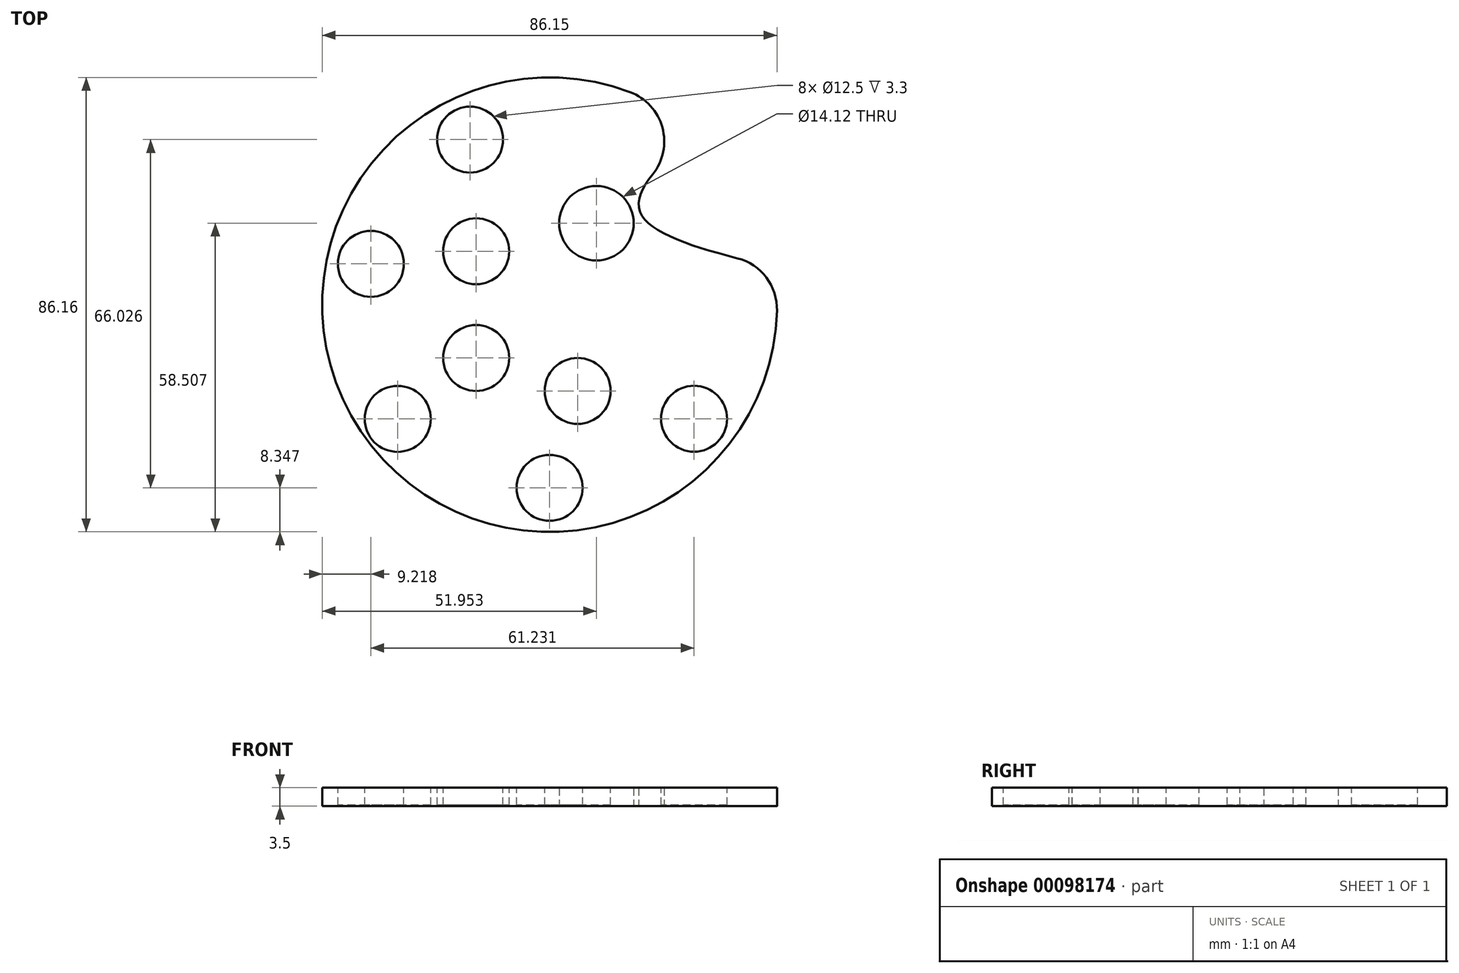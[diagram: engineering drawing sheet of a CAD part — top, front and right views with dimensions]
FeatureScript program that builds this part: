
annotation { "Feature Type Name" : "Feature", "Feature Type Description" : "" }
export const myFeature = defineFeature(function(context is Context, id is Id, definition is map)
    precondition{}
    {
        {
            var Q0;
            Q0=qCreatedBy(makeId("Top.planeOp"),FACE);
            var sketch = newSketch(context, id + "F0", { "sketchPlane" : qUnion([Q0])});
            skArc(sketch, "E0", {"start": v(27.73, 32.97) * mm, "mid": v(-37.42, -21.34) * mm, "end": v(42.5, 7.08) * mm});
            skFitSpline(sketch, "E1", {"points": [v(27.73, 32.97) * mm, v(17, 17.93) * mm, v(42.5, 7.08) * mm], "startDerivative": vector(-39.63, -36.53) * mm, "endDerivative": vector(65.58, -15.93) * mm});
            skSolve(sketch);
        }
        {
            var Q0;
            Q0 = qSketchRegion(id + "F0", true);
            extrude(context, id + "F1", {"entities" : qUnion([Q0]), "depth" : 3.5 * mm});
        }
        {
            var Q0;
            Q0=qCreatedBy(makeId("Top.planeOp"),FACE);
            var sketch = newSketch(context, id + "F2", { "sketchPlane" : qUnion([Q0])});
            skCircle(sketch, "E2", {"center": v(8.87, 15.43) * mm, "radius": 7.06 * mm});
            skSolve(sketch);
        }
        {
            var Q0;
            Q0=makeQuery(id+"F2.imprint","IMPRINT",FACE,{"disambiguationData":[TD([[makeQuery(id+"F2.imprint","IMPRINT",EDGE,{"derivedFrom":sQuery(id+"F2.wireOp",EDGE,"E2")}),1.0]])]});
            extrude(context, id + "F3", {"entities" : qUnion([Q0]), "operationType" : NewBodyOperationType.REMOVE, "depth" : 25 * mm});
        }
        {
            var Q0;
            Q0=makeQuery(id+"F1.opExtrude","CAP_FACE",FACE,{"disambiguationData":[OSD([sQuery(id+"F0.wireOp",EDGE,"E0"),sQuery(id+"F0.wireOp",EDGE,"E1")])],"isStart":false});
            var sketch = newSketch(context, id + "F4", { "sketchPlane" : qUnion([Q0])});
            skCircle(sketch, "E3.cCircle", {"center": v(0, 0) * mm, "radius": 31.3 * mm, "construction": true});
            skLineSegment(sketch, "E3.0", {"start": v(-15.07, 31.3) * mm, "end": v(15.07, 31.3) * mm, "construction": true});
            skLineSegment(sketch, "E3.1", {"start": v(15.07, 31.3) * mm, "end": v(33.86, 7.73) * mm, "construction": true});
            skLineSegment(sketch, "E3.2", {"start": v(33.86, 7.73) * mm, "end": v(27.16, -21.66) * mm, "construction": true});
            skLineSegment(sketch, "E3.3", {"start": v(27.16, -21.66) * mm, "end": v(0, -34.73) * mm, "construction": true});
            skLineSegment(sketch, "E3.4", {"start": v(0, -34.73) * mm, "end": v(-27.16, -21.66) * mm, "construction": true});
            skLineSegment(sketch, "E3.5", {"start": v(-27.16, -21.66) * mm, "end": v(-33.86, 7.73) * mm, "construction": true});
            skLineSegment(sketch, "E3.6", {"start": v(-33.86, 7.73) * mm, "end": v(-15.07, 31.3) * mm, "construction": true});
            skPoint(sketch, "E3.0.midPoint", {"position": v(0, 31.3) * mm});
            skCircle(sketch, "E4", {"center": v(-15.07, 31.3) * mm, "radius": 6.25 * mm});
            skCircle(sketch, "E5", {"center": v(-33.86, 7.73) * mm, "radius": 6.25 * mm});
            skCircle(sketch, "E6", {"center": v(-28.78, -21.66) * mm, "radius": 6.25 * mm});
            skCircle(sketch, "E7", {"center": v(0, -34.73) * mm, "radius": 6.25 * mm});
            skCircle(sketch, "E8", {"center": v(27.37, -21.63) * mm, "radius": 6.25 * mm});
            skSolve(sketch);
        }
        {
            var Q0;
            Q0 = qSketchRegion(id + "F4", true);
            extrude(context, id + "F5", {"entities" : qUnion([Q0]), "operationType" : NewBodyOperationType.REMOVE, "oppositeDirection" : true, "depth" : 3.3 * mm});
        }
        {
            var Q0;
            Q0=makeQuery(id+"F1.opExtrude","CAP_FACE",FACE,{"disambiguationData":[OSD([sQuery(id+"F0.wireOp",EDGE,"E0"),sQuery(id+"F0.wireOp",EDGE,"E1")])],"isStart":false});
            var sketch = newSketch(context, id + "F6", { "sketchPlane" : qUnion([Q0])});
            skCircle(sketch, "E9.cCircle", {"center": v(0, 0) * mm, "radius": 16.36 * mm, "construction": true});
            skLineSegment(sketch, "E9.0", {"start": v(-5.32, 16.36) * mm, "end": v(5.32, 16.36) * mm, "construction": true});
            skLineSegment(sketch, "E9.1", {"start": v(5.32, 16.36) * mm, "end": v(13.92, 10.11) * mm, "construction": true});
            skLineSegment(sketch, "E9.2", {"start": v(13.92, 10.11) * mm, "end": v(17.2, 0) * mm, "construction": true});
            skLineSegment(sketch, "E9.3", {"start": v(17.2, 0) * mm, "end": v(13.92, -10.11) * mm, "construction": true});
            skLineSegment(sketch, "E9.4", {"start": v(13.92, -10.11) * mm, "end": v(5.32, -16.36) * mm, "construction": true});
            skLineSegment(sketch, "E9.5", {"start": v(5.32, -16.36) * mm, "end": v(-5.32, -16.36) * mm, "construction": true});
            skLineSegment(sketch, "E9.6", {"start": v(-5.32, -16.36) * mm, "end": v(-13.92, -10.11) * mm, "construction": true});
            skLineSegment(sketch, "E9.7", {"start": v(-13.92, -10.11) * mm, "end": v(-17.2, 0) * mm, "construction": true});
            skLineSegment(sketch, "E9.8", {"start": v(-17.2, 0) * mm, "end": v(-13.92, 10.11) * mm, "construction": true});
            skLineSegment(sketch, "E9.9", {"start": v(-13.92, 10.11) * mm, "end": v(-5.32, 16.36) * mm, "construction": true});
            skPoint(sketch, "E9.0.midPoint", {"position": v(0, 16.36) * mm});
            skCircle(sketch, "E10", {"center": v(-13.92, -10.11) * mm, "radius": 6.25 * mm});
            skCircle(sketch, "E11", {"center": v(5.32, -16.36) * mm, "radius": 6.25 * mm});
            skCircle(sketch, "E12", {"center": v(-13.92, 10.11) * mm, "radius": 6.25 * mm});
            skArc(sketch, "E13", {"start": v(15.45, -5.38) * mm, "mid": v(15.45, -5.38) * mm, "end": v(15.46, -5.38) * mm});
            skArc(sketch, "E14.trimOffspring", {"start": v(15.46, 5.38) * mm, "mid": v(15.45, 5.38) * mm, "end": v(15.45, 5.38) * mm});
            skSolve(sketch);
        }
        {
            var Q0;
            Q0 = qSketchRegion(id + "F6", true);
            extrude(context, id + "F7", {"entities" : qUnion([Q0]), "operationType" : NewBodyOperationType.REMOVE, "oppositeDirection" : true, "depth" : 3.3 * mm});
        }
        {
            var Q0;
            {var subQ0=sQuery(id+"F0.wireOp",EDGE,"E1");var subQ1=sQuery(id+"F0.wireOp",EDGE,"E0");Q0=makeQuery(id+"F1.opExtrude","SWEPT_EDGE",EDGE,{"disambiguationData":[OSD([subQ1,subQ0]),TDD([makeQuery(id+"F0.imprint","INTERSECT",VERTEX,{"disambiguationData":[OD(0.0)],"derivedFrom":[subQ1,subQ0]})])]});}
            var Q1;
            {var subQ0=sQuery(id+"F0.wireOp",EDGE,"E1");var subQ1=sQuery(id+"F0.wireOp",EDGE,"E0");Q1=makeQuery(id+"F1.opExtrude","SWEPT_EDGE",EDGE,{"disambiguationData":[OSD([subQ1,subQ0]),TDD([makeQuery(id+"F0.imprint","INTERSECT",VERTEX,{"disambiguationData":[OD(1.0)],"derivedFrom":[subQ1,subQ0]})])]});}
            fillet(context, id + "F8", {"entities" : qUnion([Q0, Q1]), "radius" : 10 * mm, "tangentPropagation" : true, "allowEdgeOverflow" : false});
        }
    });
